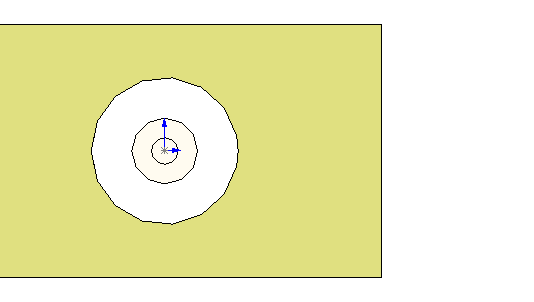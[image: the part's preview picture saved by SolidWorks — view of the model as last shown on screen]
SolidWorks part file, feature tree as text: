
SOLIDWORKS PART (.sldprt)
format: sldprt  version: not decoded by parser v0  size: 165,376 bytes
history: native  units: mm
features: sketch x5, extrude x5 (+11 scaffold rows collapsed; 1 parser-record rows omitted)
feature tree (22):
  scaffold x11  (default folders/planes/origin — collapsed)
  parser-record x1  (decoder bookkeeping rows leaked as tree rows — omitted from the tree; the rows remain in map.json)
  sketch  "Sketch1"  dims[D1=22.225mm]
  extrude  "Extrude1"  Depth=52.197mm
  sketch  "Sketch2"  dims[D1=9.9568mm]
  extrude  "Extrude2"  Depth=3.937mm
  sketch  "Sketch4"  dims[D1=4.0132mm]
  extrude  "Extrude3"  Depth=19.05mm
  sketch  "Sketch5"  dims[D1=38.1mm D2=65.532mm D3=32.766mm D4=19.05mm]
  extrude  "Extrude4"  Depth=3.175mm
  sketch  "Sketch6"  dims[D1=38.608mm D2=25.8572mm D3=4.572mm D4=12.7mm]
  extrude  "Extrude5"  Depth=23.114mm
decode coverage: 10 of 10 modeling features carry decoded parameters
note: suppression state not decoded; provenance and decode notes live in map.json
